# Revit family: 13995 Комплект мебели «Лотос» Хоббика
name_source: partatom
category: Антураж
revit_build: Autodesk Revit 2018 (Build: 20180423_1000(x64)
units: mm (PartAtom-declared; Revit-internal decimal feet)

## family parameters
Всегда вертикально = Да
Источник визуального образа = Геометрия семейства
На основе рабочей плоскости = Нет
Общий = Нет
При загрузке вырезать с полостями = Нет
Точка расчета площади = Нет

## types (2) — shared parameters
URL = https://hobbyka.ru
Артикул товара = Арт. 13995
Группа модели = Комплекты садовой мебели
Изготовитель = ООО «Хоббика»
Изображение типоразмера = Комплект мебели «Лотос» Арт 13995.jpg
Материал изделия = Бетон, дерево
Цвет основания = Бетон

## per-type parameters (varying)
| type | Высота | Длина | Пуф | Стол | Цвет сидения | Ширина |
| Комплект мебели «Лотос». Стол | 750 мм | 1000 мм | Нет | Да | <По категории> | 1000 мм |
| Комплект мебели «Лотос». Пуф | 470 мм | 350 мм | Да | Нет | Дерево | 350 мм |

note: column(s) folded — value = type name in every type: Описание
